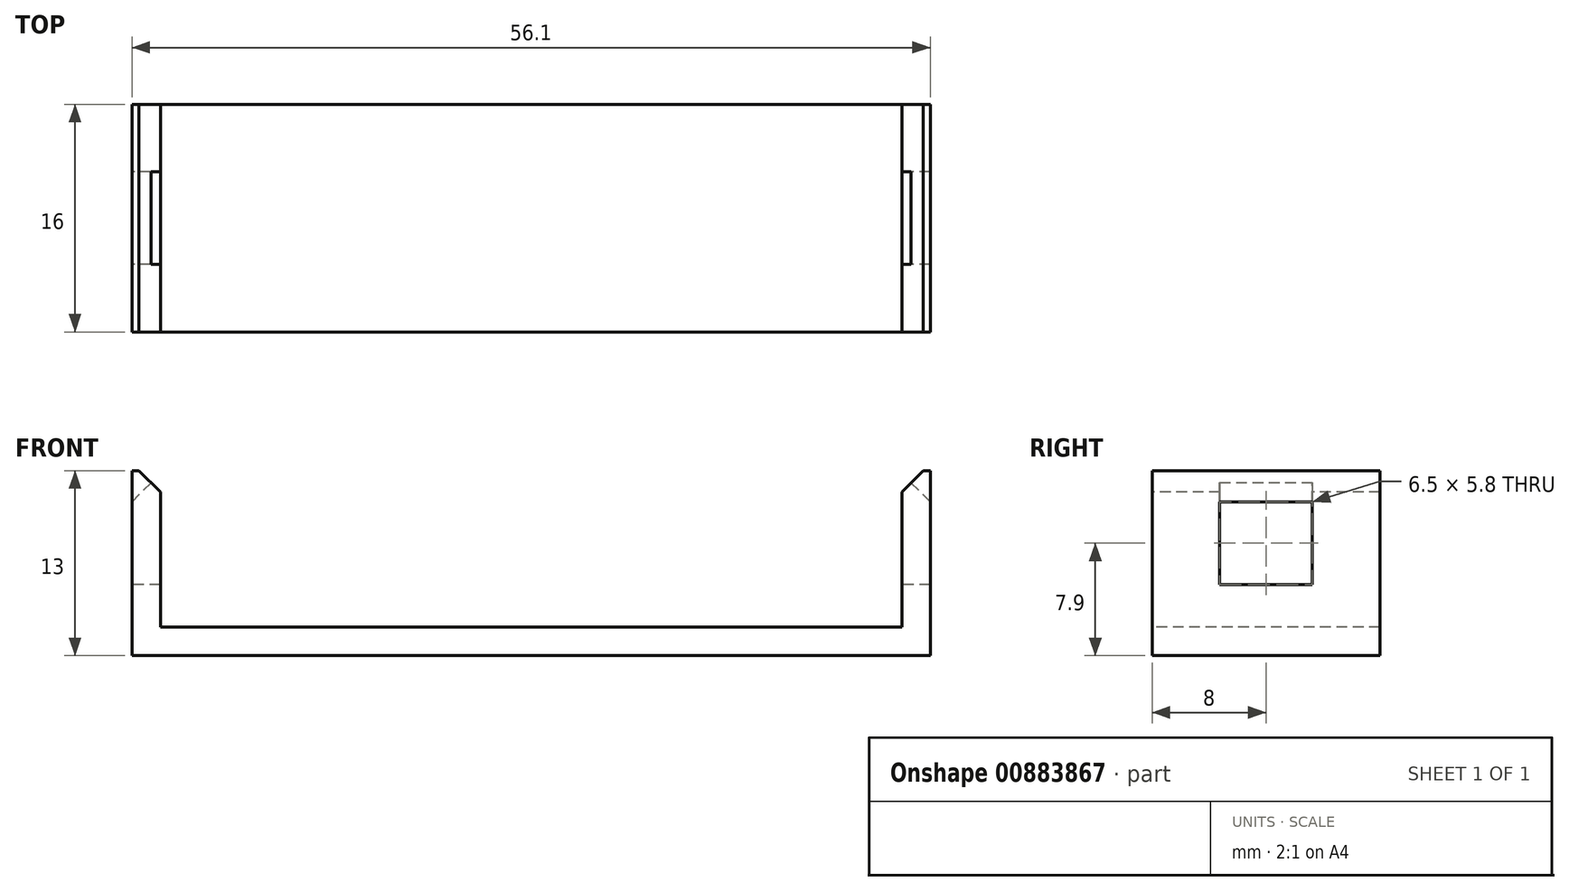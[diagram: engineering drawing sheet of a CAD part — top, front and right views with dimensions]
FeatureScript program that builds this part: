
annotation { "Feature Type Name" : "Feature", "Feature Type Description" : "" }
export const myFeature = defineFeature(function(context is Context, id is Id, definition is map)
    precondition{}
    {
        {
            var Q0;
            Q0=qCreatedBy(makeId("Top.planeOp"),FACE);
            var sketch = newSketch(context, id + "F0", { "sketchPlane" : qUnion([Q0])});
            skLineSegment(sketch, "E0.bottom", {"start": v(0, 0) * mm, "end": v(52.1, 0) * mm});
            skLineSegment(sketch, "E0.top", {"start": v(0, -16) * mm, "end": v(52.1, -16) * mm});
            skLineSegment(sketch, "E0.left", {"start": v(0, 0) * mm, "end": v(0, -16) * mm});
            skLineSegment(sketch, "E0.right", {"start": v(52.1, 0) * mm, "end": v(52.1, -16) * mm});
            skSolve(sketch);
        }
        {
            var Q0;
            Q0=makeQuery(id+"F0.imprint","IMPRINT",FACE,{"disambiguationData":[TD([[makeQuery(id+"F0.imprint","IMPRINT",EDGE,{"derivedFrom":sQuery(id+"F0.wireOp",EDGE,"E0.bottom")}),-1.0]])]});
            extrude(context, id + "F1", {"entities" : qUnion([Q0]), "depth" : 5 * mm, "offsetDistance" : 25 * mm});
        }
        {
            var Q0;
            Q0=qCreatedBy(makeId("Top.planeOp"),FACE);
            var sketch = newSketch(context, id + "F2", { "sketchPlane" : qUnion([Q0])});
            skLineSegment(sketch, "E1.bottom", {"start": v(0, 0) * mm, "end": v(-2, 0) * mm});
            skLineSegment(sketch, "E1.top", {"start": v(0, -16) * mm, "end": v(-2, -16) * mm});
            skLineSegment(sketch, "E1.left", {"start": v(0, 0) * mm, "end": v(0, -16) * mm});
            skLineSegment(sketch, "E1.right", {"start": v(-2, 0) * mm, "end": v(-2, -16) * mm});
            skLineSegment(sketch, "E2.bottom", {"start": v(52.1, -16) * mm, "end": v(54.1, -16) * mm});
            skLineSegment(sketch, "E2.top", {"start": v(52.1, 0) * mm, "end": v(54.1, 0) * mm});
            skLineSegment(sketch, "E2.left", {"start": v(52.1, -16) * mm, "end": v(52.1, 0) * mm});
            skLineSegment(sketch, "E2.right", {"start": v(54.1, -16) * mm, "end": v(54.1, 0) * mm});
            skSolve(sketch);
        }
        {
            var Q0;
            Q0=makeQuery(id+"F2.imprint","IMPRINT",FACE,{"disambiguationData":[TD([[makeQuery(id+"F2.imprint","IMPRINT",EDGE,{"derivedFrom":sQuery(id+"F2.wireOp",EDGE,"E1.bottom")}),1.0]])]});
            var Q1;
            Q1=makeQuery(id+"F2.imprint","IMPRINT",FACE,{"disambiguationData":[TD([[makeQuery(id+"F2.imprint","IMPRINT",EDGE,{"derivedFrom":sQuery(id+"F2.wireOp",EDGE,"E2.bottom")}),1.0]])]});
            extrude(context, id + "F3", {"entities" : qUnion([Q0, Q1]), "operationType" : NewBodyOperationType.ADD, "depth" : 16 * mm, "offsetDistance" : 25 * mm});
        }
        {
            var Q0;
            Q0=makeQuery(id+"F3.opExtrude","SWEPT_FACE",FACE,{"disambiguationData":[OSD([sQuery(id+"F2.wireOp",EDGE,"E2.left")])]});
            var sketch = newSketch(context, id + "F4", { "sketchPlane" : qUnion([Q0])});
            skLineSegment(sketch, "E3", {"start": v(0, 16) * mm, "end": v(8, 16) * mm, "construction": true});
            skLineSegment(sketch, "E4", {"start": v(8, 5) * mm, "end": v(8, 13.3) * mm, "construction": true});
            skLineSegment(sketch, "E5", {"start": v(8, 13.3) * mm, "end": v(11.6, 13.3) * mm, "construction": true});
            skLineSegment(sketch, "E6.bottom", {"start": v(11.25, 13.3) * mm, "end": v(4.78, 13.3) * mm, "construction": true});
            skLineSegment(sketch, "E6.top", {"start": v(11.25, 11.69) * mm, "end": v(4.78, 11.69) * mm, "construction": true});
            skLineSegment(sketch, "E6.left", {"start": v(11.25, 13.3) * mm, "end": v(11.25, 11.69) * mm, "construction": true});
            skLineSegment(sketch, "E6.right", {"start": v(4.78, 13.3) * mm, "end": v(4.78, 11.69) * mm, "construction": true});
            skLineSegment(sketch, "E7.bottom", {"start": v(11.25, 13.3) * mm, "end": v(4.75, 13.3) * mm});
            skLineSegment(sketch, "E7.top", {"start": v(11.25, 8) * mm, "end": v(4.75, 8) * mm});
            skLineSegment(sketch, "E7.left", {"start": v(11.25, 13.3) * mm, "end": v(11.25, 8) * mm});
            skLineSegment(sketch, "E7.right", {"start": v(4.75, 13.3) * mm, "end": v(4.75, 8) * mm});
            skSolve(sketch);
        }
        {
            var Q0;
            Q0=makeQuery(id+"F4.imprint","IMPRINT",FACE,{"disambiguationData":[TD([[makeQuery(id+"F4.imprint","IMPRINT",EDGE,{"derivedFrom":sQuery(id+"F4.wireOp",EDGE,"E7.bottom")}),1.0]])]});
            extrude(context, id + "F5", {"entities" : qUnion([Q0]), "operationType" : NewBodyOperationType.REMOVE, "endBound" : BoundingType.SYMMETRIC, "oppositeDirection" : true, "depth" : 390 * mm, "offsetDistance" : 25 * mm});
        }
        {
            var Q0;
            Q0=makeQuery(id+"F3.opExtrude","CAP_EDGE",EDGE,{"disambiguationData":[OSD([sQuery(id+"F2.wireOp",EDGE,"E2.left")])],"isStart":false});
            var Q1;
            Q1=makeQuery(id+"F3.opExtrude","CAP_EDGE",EDGE,{"disambiguationData":[OSD([sQuery(id+"F2.wireOp",EDGE,"E1.left")])],"isStart":false});
            chamfer(context, id + "F6", {"entities" : qUnion([Q0, Q1]), "width" : 1.5 * mm, "tangentPropagation" : true});
        }
        {
            var Q0;
            Q0=makeQuery(id+"F5.boolean.opBoolean","INTERSECT",EDGE,{"derivedFrom":[makeQuery(id+"F3.opExtrude","SWEPT_FACE",FACE,{"disambiguationData":[OSD([sQuery(id+"F2.wireOp",EDGE,"E2.left")])]}),makeQuery(id+"F5.opExtrude","SWEPT_FACE",FACE,{"disambiguationData":[OSD([sQuery(id+"F4.wireOp",EDGE,"E7.bottom")])]})]});
            var Q1;
            Q1=makeQuery(id+"F5.boolean.opBoolean","INTERSECT",EDGE,{"derivedFrom":[makeQuery(id+"F3.opExtrude","SWEPT_FACE",FACE,{"disambiguationData":[OSD([sQuery(id+"F2.wireOp",EDGE,"E1.left")])]}),makeQuery(id+"F5.opExtrude","SWEPT_FACE",FACE,{"disambiguationData":[OSD([sQuery(id+"F4.wireOp",EDGE,"E7.bottom")])]})]});
            chamfer(context, id + "F7", {"entities" : qUnion([Q0, Q1]), "width" : 2.5 * mm, "tangentPropagation" : true});
        }
        {
            var Q0;
            Q0=makeQuery(id+"F3.boolean.opBoolean","MERGE",FACE,{"derivedFrom":[makeQuery(id+"F1.opExtrude","CAP_FACE",FACE,{"disambiguationData":[OSD([sQuery(id+"F0.wireOp",EDGE,"E0.bottom"),sQuery(id+"F0.wireOp",EDGE,"E0.top"),sQuery(id+"F0.wireOp",EDGE,"E0.left"),sQuery(id+"F0.wireOp",EDGE,"E0.right")])],"isStart":true}),makeQuery(id+"F3.opExtrude","CAP_FACE",FACE,{"disambiguationData":[OSD([sQuery(id+"F2.wireOp",EDGE,"E1.bottom"),sQuery(id+"F2.wireOp",EDGE,"E1.top"),sQuery(id+"F2.wireOp",EDGE,"E1.left"),sQuery(id+"F2.wireOp",EDGE,"E1.right")])],"isStart":true}),makeQuery(id+"F3.opExtrude","CAP_FACE",FACE,{"disambiguationData":[OSD([sQuery(id+"F2.wireOp",EDGE,"E2.bottom"),sQuery(id+"F2.wireOp",EDGE,"E2.top"),sQuery(id+"F2.wireOp",EDGE,"E2.left"),sQuery(id+"F2.wireOp",EDGE,"E2.right")])],"isStart":true})]});
            extrude(context, id + "F8", {"entities" : qUnion([Q0]), "operationType" : NewBodyOperationType.REMOVE, "oppositeDirection" : true, "depth" : 3 * mm, "offsetDistance" : 25 * mm});
        }
    });
